# Revit family: VENTS-VKPF
name_source: partatom
category: Mechanical Equipment
units: mm (PartAtom-declared; Revit-internal decimal feet)

## family parameters
Always vertical = Yes
Classification = None
Cut with Voids When Loaded = No
OmniClass Number = 23.75.35.17.11
OmniClass Title = Fans for Air Ductwork
Part Type = Breaks Into
Room Calculation Point = No
Round Connector Dimension = Use Diameter
Shared = No
Work Plane-Based = No

## types (16) — shared parameters
Casing Material = Fan Zinc
Description = Inline centrifugal fan for rectangular ducts
Family Version = 1.0
Load Classification = HVAC
Maintenance Zone Height = 600 mm
Maintenance Zone Material = Maintenance Zone
Manufacturer = Vents
Power Factor = 1
Protection rating = IP X4
URL = https://ventilation-system.com
dFl = 20 mm  [stored 0.0656168 ft]

## per-type parameters (varying)
- VKPF 4Е 400х200: Apparent Power=295 VA; B=400 mm; B2=440 mm; Connection H=200 mm  [stored 0.656168 ft]; Connection W=400 mm; Current=1 A; DistributionBox=No; H=200 mm  [stored 0.656168 ft]; H2=240 mm  [stored 0.787402 ft]; H3=255 mm  [stored 0.836614 ft]; L=500 mm; Maintenance Zone Length=500 mm; Maintenance Zone Width=400 mm; Maximum Air Flow=1440 m³/h; Noise Level at 3 m (dBa)=50; Number of Poles=1; Power=295 W; RPM (min-1)=1350; Transported Air Temperature (°C)=-25...+40; Type Comments=Inline centrifugal fan VKPF 4Е 400х200; Voltage=230 V; Weight=17.50 kg; eL=118 mm; eW=310 mm  [stored 1.01706 ft]; gsD=200 mm  [stored 0.656168 ft]; mL=346 mm; mR1=105 mm  [stored 0.344488 ft]; mR2=76 mm  [stored 0.249344 ft]; mR3=38 mm  [stored 0.124672 ft]; mW=225 mm  [stored 0.738189 ft]
- VKPF 4D 400х200: Apparent Power=282 VA; B=400 mm; B2=440 mm; Connection H=200 mm  [stored 0.656168 ft]; Connection W=400 mm; Current=1 A; DistributionBox=No; H=200 mm  [stored 0.656168 ft]; H2=240 mm  [stored 0.787402 ft]; H3=255 mm  [stored 0.836614 ft]; L=500 mm; Maintenance Zone Length=500 mm; Maintenance Zone Width=400 mm; Maximum Air Flow=1470 m³/h; Noise Level at 3 m (dBa)=52; Number of Poles=3; Power=282 W; RPM (min-1)=1300; Transported Air Temperature (°C)=-25...+45; Type Comments=Inline centrifugal fan VKPF 4D 400х200; Voltage=400 V; Weight=17.50 kg; eL=118 mm; eW=310 mm  [stored 1.01706 ft]; gsD=200 mm  [stored 0.656168 ft]; mL=346 mm; mR1=105 mm  [stored 0.344488 ft]; mR2=76 mm  [stored 0.249344 ft]; mR3=38 mm  [stored 0.124672 ft]; mW=225 mm  [stored 0.738189 ft]
- VKPF 4Е 500х250: Apparent Power=535 VA; B=500 mm; B2=540 mm; Connection H=250 mm  [stored 0.82021 ft]; Connection W=500 mm; Current=2 A; DistributionBox=No; H=250 mm  [stored 0.82021 ft]; H2=290 mm  [stored 0.951444 ft]; H3=310 mm  [stored 1.01706 ft]; L=640 mm; Maintenance Zone Length=640 mm; Maintenance Zone Width=500 mm; Maximum Air Flow=1750 m³/h; Noise Level at 3 m (dBa)=53; Number of Poles=1; Power=535 W; RPM (min-1)=1250; Transported Air Temperature (°C)=-20...+40; Type Comments=Inline centrifugal fan VKPF 4Е 500х250; Voltage=230 V; Weight=24.00 kg; eL=150 mm; eW=412 mm; gsD=250 mm  [stored 0.82021 ft]; mL=461 mm; mR1=114 mm  [stored 0.374016 ft]; mR2=87 mm  [stored 0.285433 ft]; mR3=47 mm  [stored 0.154199 ft]; mW=258 mm  [stored 0.846457 ft]
- VKPF 4D 500х250: Apparent Power=570 VA; B=500 mm; B2=540 mm; Connection H=250 mm  [stored 0.82021 ft]; Connection W=500 mm; Current=1 A; DistributionBox=No; H=250 mm  [stored 0.82021 ft]; H2=290 mm  [stored 0.951444 ft]; H3=310 mm  [stored 1.01706 ft]; L=640 mm; Maintenance Zone Length=640 mm; Maintenance Zone Width=500 mm; Maximum Air Flow=1850 m³/h; Noise Level at 3 m (dBa)=54; Number of Poles=3; Power=570 W; RPM (min-1)=1270; Transported Air Temperature (°C)=-20...+40; Type Comments=Inline centrifugal fan VKPF 4D 500х250; Voltage=400 V; Weight=24.00 kg; eL=150 mm; eW=412 mm; gsD=250 mm  [stored 0.82021 ft]; mL=461 mm; mR1=114 mm  [stored 0.374016 ft]; mR2=87 mm  [stored 0.285433 ft]; mR3=47 mm  [stored 0.154199 ft]; mW=258 mm  [stored 0.846457 ft]
- VKPF 4Е 500х300: Apparent Power=710 VA; B=500 mm; B2=540 mm; Connection H=300 mm; Connection W=500 mm; Current=3 A; DistributionBox=No; H=300 mm; H2=340 mm  [stored 1.11549 ft]; H3=365 mm; L=680 mm; Maintenance Zone Length=680 mm; Maintenance Zone Width=500 mm; Maximum Air Flow=2350 m³/h; Noise Level at 3 m (dBa)=57; Number of Poles=1; Power=710 W; RPM (min-1)=1230; Transported Air Temperature (°C)=-25...+70; Type Comments=Inline centrifugal fan VKPF 4Е 500х300; Voltage=230 V; Weight=33.00 kg; eL=170 mm  [stored 0.557743 ft]; eW=370 mm; gsD=250 mm  [stored 0.82021 ft]; mL=495 mm; mR1=126 mm  [stored 0.413386 ft]; mR2=95 mm  [stored 0.31168 ft]; mR3=47 mm  [stored 0.154199 ft]; mW=284 mm  [stored 0.931759 ft]
- VKPF 4D 500х300: Apparent Power=855 VA; B=500 mm; B2=540 mm; Connection H=300 mm; Connection W=500 mm; Current=2 A; DistributionBox=No; H=300 mm; H2=340 mm  [stored 1.11549 ft]; H3=365 mm; L=680 mm; Maintenance Zone Length=680 mm; Maintenance Zone Width=500 mm; Maximum Air Flow=2350 m³/h; Noise Level at 3 m (dBa)=56; Number of Poles=3; Power=855 W; RPM (min-1)=1300; Transported Air Temperature (°C)=-25...+50; Type Comments=Inline centrifugal fan VKPF 4D 500х300; Voltage=400 V; Weight=33.00 kg; eL=170 mm  [stored 0.557743 ft]; eW=370 mm; gsD=250 mm  [stored 0.82021 ft]; mL=495 mm; mR1=126 mm  [stored 0.413386 ft]; mR2=95 mm  [stored 0.31168 ft]; mR3=47 mm  [stored 0.154199 ft]; mW=284 mm  [stored 0.931759 ft]
- VKPF 4Е 600х300: Apparent Power=1240 VA; B=600 mm; B2=640 mm; Connection H=300 mm; Connection W=600 mm; Current=6 A; DistributionBox=No; H=300 mm; H2=340 mm  [stored 1.11549 ft]; H3=375 mm; L=680 mm; Maintenance Zone Length=680 mm; Maintenance Zone Width=600 mm; Maximum Air Flow=2950 m³/h; Noise Level at 3 m (dBa)=59; Number of Poles=1; Power=1240 W; RPM (min-1)=1210; Transported Air Temperature (°C)=-25...+50; Type Comments=Inline centrifugal fan VKPF 4Е 600х300; Voltage=230 V; Weight=35.00 kg; eL=117 mm  [stored 0.383858 ft]; eW=495 mm; gsD=300 mm; mL=462 mm; mR1=148 mm  [stored 0.485564 ft]; mR2=110 mm  [stored 0.360892 ft]; mR3=68 mm; mW=308 mm  [stored 1.0105 ft]
- VKPF 4D 600х300: Apparent Power=1560 VA; B=600 mm; B2=640 mm; Connection H=300 mm; Connection W=600 mm; Current=3 A; DistributionBox=No; H=300 mm; H2=340 mm  [stored 1.11549 ft]; H3=375 mm; L=680 mm; Maintenance Zone Length=680 mm; Maintenance Zone Width=600 mm; Maximum Air Flow=3740 m³/h; Noise Level at 3 m (dBa)=57; Number of Poles=3; Power=1560 W; RPM (min-1)=1310; Transported Air Temperature (°C)=-25...+65; Type Comments=Inline centrifugal fan VKPF 4D 600х300; Voltage=400 V; Weight=35.00 kg; eL=117 mm  [stored 0.383858 ft]; eW=495 mm; gsD=300 mm; mL=462 mm; mR1=148 mm  [stored 0.485564 ft]; mR2=110 mm  [stored 0.360892 ft]; mR3=68 mm; mW=308 mm  [stored 1.0105 ft]
- VKPF 4Е 600х350: Apparent Power=2480 VA; B=600 mm; B2=640 mm; Connection H=350 mm; Connection W=600 mm; Current=14 A; DistributionBox=No; H=350 mm; H2=390 mm; H3=425 mm; L=735 mm; Maintenance Zone Length=735 mm; Maintenance Zone Width=600 mm; Maximum Air Flow=4260 m³/h; Noise Level at 3 m (dBa)=59; Number of Poles=1; Power=2480 W; RPM (min-1)=1260; Transported Air Temperature (°C)=-20...+40; Type Comments=Inline centrifugal fan VKPF 4Е 600х350; Voltage=230 V; Weight=49.50 kg; eL=180 mm  [stored 0.590551 ft]; eW=495 mm; gsD=300 mm; mL=504 mm; mR1=162 mm  [stored 0.531496 ft]; mR2=120 mm  [stored 0.393701 ft]; mR3=68 mm; mW=353 mm
- VKPF 4D 600х350: Apparent Power=2460 VA; B=600 mm; B2=640 mm; Connection H=350 mm; Connection W=600 mm; Current=4 A; DistributionBox=No; H=350 mm; H2=390 mm; H3=425 mm; L=735 mm; Maintenance Zone Length=735 mm; Maintenance Zone Width=600 mm; Maximum Air Flow=5020 m³/h; Noise Level at 3 m (dBa)=60; Number of Poles=3; Power=2460 W; RPM (min-1)=1300; Transported Air Temperature (°C)=-20...+40; Type Comments=Inline centrifugal fan VKPF 4D 600х350; Voltage=400 V; Weight=49.50 kg; eL=180 mm  [stored 0.590551 ft]; eW=495 mm; gsD=300 mm; mL=504 mm; mR1=162 mm  [stored 0.531496 ft]; mR2=120 mm  [stored 0.393701 ft]; mR3=68 mm; mW=353 mm
- VKPF 4D 700х400: Apparent Power=3630 VA; B=700 mm; B2=740 mm; Connection H=400 mm; Connection W=700 mm; Current=6 A; DistributionBox=Yes; H=400 mm; H2=440 mm; H3=480 mm; L=780 mm; Maintenance Zone Length=780 mm; Maintenance Zone Width=700 mm; Maximum Air Flow=6450 m³/h; Noise Level at 3 m (dBa)=65; Number of Poles=3; Power=3630 W; RPM (min-1)=1320; Transported Air Temperature (°C)=-25...+40; Type Comments=Inline centrifugal fan VKPF 4D 700х400; Voltage=400 V; Weight=60.00 kg; eL=180 mm  [stored 0.590551 ft]; eW=100 mm  [stored 0.328084 ft]; gsD=350 mm; mL=520 mm; mR1=172 mm  [stored 0.564304 ft]; mR2=130 mm  [stored 0.426509 ft]; mR3=78 mm  [stored 0.255906 ft]; mW=402 mm
- VKPF 6D 700х400: Apparent Power=1150 VA; B=700 mm; B2=740 mm; Connection H=400 mm; Connection W=700 mm; Current=2 A; DistributionBox=Yes; H=400 mm; H2=440 mm; H3=480 mm; L=780 mm; Maintenance Zone Length=780 mm; Maintenance Zone Width=700 mm; Maximum Air Flow=4050 m³/h; Noise Level at 3 m (dBa)=58; Number of Poles=3; Power=1150 W; RPM (min-1)=890; Transported Air Temperature (°C)=-20...+70; Type Comments=Inline centrifugal fan VKPF 6D 700х400; Voltage=400 V; Weight=56.00 kg; eL=180 mm  [stored 0.590551 ft]; eW=100 mm  [stored 0.328084 ft]; gsD=350 mm; mL=520 mm; mR1=172 mm  [stored 0.564304 ft]; mR2=130 mm  [stored 0.426509 ft]; mR3=78 mm  [stored 0.255906 ft]; mW=402 mm
- VKPF 4D 800х500: Apparent Power=5850 VA; B=800 mm; B2=840 mm; Connection H=500 mm; Connection W=800 mm; Current=9 A; DistributionBox=Yes; H=500 mm; H2=540 mm; H3=580 mm; L=880 mm; Maintenance Zone Length=880 mm; Maintenance Zone Width=800 mm; Maximum Air Flow=8120 m³/h; Noise Level at 3 m (dBa)=67; Number of Poles=3; Power=5850 W; RPM (min-1)=1140; Transported Air Temperature (°C)=-25...+40; Type Comments=Inline centrifugal fan VKPF 4D 800х500; Voltage=400 V; Weight=74.00 kg; eL=210 mm  [stored 0.688976 ft]; eW=138 mm  [stored 0.452756 ft]; gsD=400 mm; mL=608 mm; mR1=202 mm  [stored 0.66273 ft]; mR2=159 mm  [stored 0.521654 ft]; mR3=78 mm  [stored 0.255906 ft]; mW=452 mm
- VKPF 6D 800х500: Apparent Power=2790 VA; B=800 mm; B2=840 mm; Connection H=500 mm; Connection W=800 mm; Current=5 A; DistributionBox=Yes; H=500 mm; H2=540 mm; H3=580 mm; L=880 mm; Maintenance Zone Length=880 mm; Maintenance Zone Width=800 mm; Maximum Air Flow=7610 m³/h; Noise Level at 3 m (dBa)=59; Number of Poles=3; Power=2790 W; RPM (min-1)=830; Transported Air Temperature (°C)=-20...+50; Type Comments=Inline centrifugal fan VKPF 6D 800х500; Voltage=400 V; Weight=70.00 kg; eL=210 mm  [stored 0.688976 ft]; eW=138 mm  [stored 0.452756 ft]; gsD=400 mm; mL=608 mm; mR1=202 mm  [stored 0.66273 ft]; mR2=159 mm  [stored 0.521654 ft]; mR3=78 mm  [stored 0.255906 ft]; mW=452 mm
- VKPF 6D 900х500: Apparent Power=3870 VA; B=900 mm; B2=940 mm; Connection H=500 mm; Connection W=900 mm; Current=7 A; DistributionBox=Yes; H=500 mm; H2=540 mm; H3=580 mm; L=954 mm; Maintenance Zone Length=954 mm; Maintenance Zone Width=900 mm; Maximum Air Flow=9540 m³/h; Noise Level at 3 m (dBa)=61; Number of Poles=3; Power=3870 W; RPM (min-1)=930; Transported Air Temperature (°C)=-20...+55; Type Comments=Inline centrifugal fan VKPF 6D 900х500; Voltage=400 V; Weight=90.00 kg; eL=200 mm  [stored 0.656168 ft]; eW=148 mm  [stored 0.485564 ft]; gsD=450 mm; mL=622 mm; mR1=240 mm  [stored 0.787402 ft]; mR2=195 mm  [stored 0.639764 ft]; mR3=78 mm  [stored 0.255906 ft]; mW=505 mm
- VKPF 6D 1000х500: Apparent Power=3870 VA; B=1000 mm; B2=1040 mm; Connection H=500 mm; Connection W=1000 mm; Current=7 A; DistributionBox=Yes; H=500 mm; H2=540 mm; H3=580 mm; L=954 mm; Maintenance Zone Length=954 mm; Maintenance Zone Width=1000 mm; Maximum Air Flow=9540 m³/h; Noise Level at 3 m (dBa)=61; Number of Poles=3; Power=3870 W; RPM (min-1)=930; Transported Air Temperature (°C)=-20...+55; Type Comments=Inline centrifugal fan VKPF 6D 1000х500; Voltage=400 V; Weight=95.00 kg; eL=200 mm  [stored 0.656168 ft]; eW=148 mm  [stored 0.485564 ft]; gsD=500 mm; mL=622 mm; mR1=240 mm  [stored 0.787402 ft]; mR2=195 mm  [stored 0.639764 ft]; mR3=78 mm  [stored 0.255906 ft]; mW=505 mm

note: column(s) folded — value = type name in every type: Model

note: [stored X ft] marks values corroborated as IEEE doubles in the binary element streams (Revit-internal decimal feet)

## geometry (parser evidence)
native form markers: Sweep x9
no freeform markers — native parametric forms only
